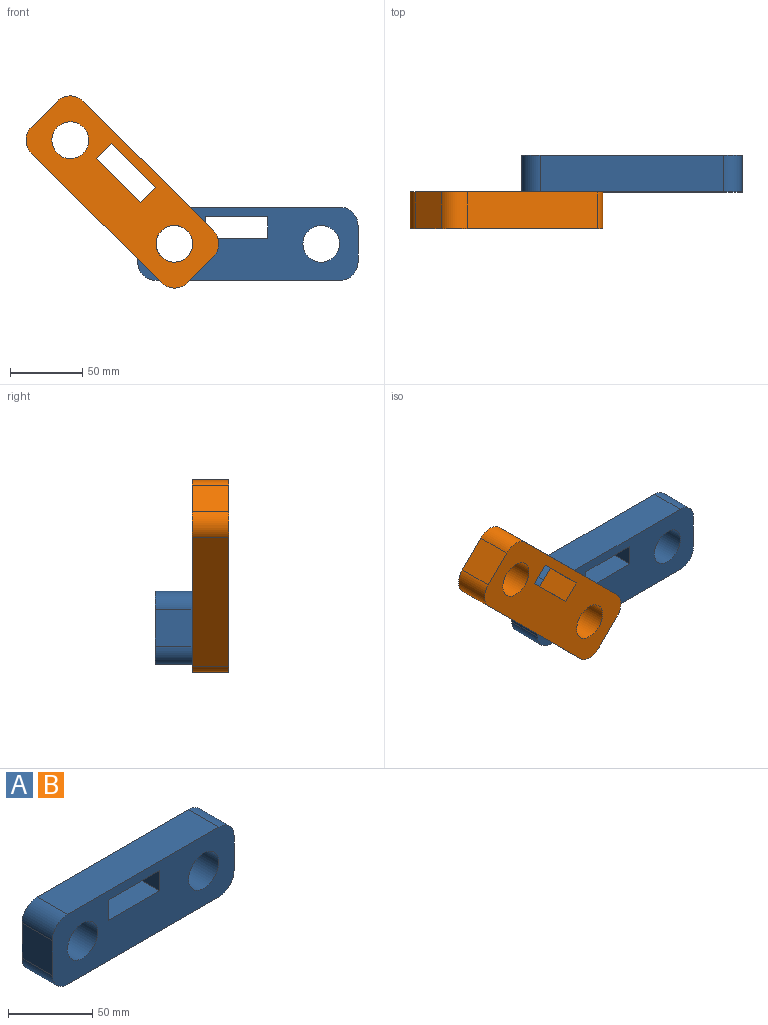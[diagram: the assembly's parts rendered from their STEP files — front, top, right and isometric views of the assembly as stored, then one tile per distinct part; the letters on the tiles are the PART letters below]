
ASSEMBLY  parts=2 mates=1
PART A: 16 faces, bbox 152.4x25.4x50.8 mm
  f0: plane 152.4x50.8mm, normal (0,-1,0), area 5955.5mm2, adj f2,f3,f4,f5,f6,f7,f8,f9
  f1: plane 152.4x50.8mm, normal (0,1,0), area 5955.5mm2, adj f2,f3,f4,f5,f6,f7,f8,f9
  f2: plane 127x25.4mm, normal (0,0,1), area 3225.8mm2, adj f0,f1,f8,f11
  f3: plane 25.4x25.4mm, normal (-1,0,0), area 645.2mm2, adj f0,f1,f8,f9
  f4: plane 127x25.4mm, normal (0,0,-1), area 3225.8mm2, adj f0,f1,f9,f10
  f5: cylinder r=12.7mm len=25.4mm, axis (0,1,0), area 2026.8mm2, adj f0,f1
  f6: cylinder r=12.7mm len=25.4mm, axis (0,1,0), area 2026.8mm2, adj f0,f1
  f7: plane 25.4x25.4mm, normal (1,0,0), area 645.2mm2, adj f0,f1,f10,f11
  f8: cylinder r=12.7mm len=25.4mm, axis (0,-1,0), area 506.7mm2, adj f0,f1,f2,f3
  f9: cylinder r=12.7mm len=25.4mm, axis (0,1,0), area 506.7mm2, adj f0,f1,f3,f4
  f10: cylinder r=12.7mm len=25.4mm, axis (0,-1,0), area 506.7mm2, adj f0,f1,f4,f7
  f11: cylinder r=12.7mm len=25.4mm, axis (0,1,0), area 506.7mm2, adj f0,f1,f2,f7
  f12: plane 42.99x25.4mm, normal (0,0,-1), area 1091.9mm2, adj f0,f1,f13,f15
  f13: plane 25.4x14.76mm, normal (1,0,0), area 374.9mm2, adj f0,f1,f12,f14
  f14: plane 42.99x25.4mm, normal (0,0,1), area 1091.9mm2, adj f0,f1,f13,f15
  f15: plane 25.4x14.76mm, normal (-1,0,0), area 374.9mm2, adj f0,f1,f12,f14
PART B: same geometry as A
PLACE A t=(-37.87,-13.28,12.88)mm fixed
PLACE B rot(axis=(0,1,0),44.9deg) t=(-124.68,-38.68,48.71)mm
MATE revolute A.f5 <-> B.f6  axis (0,1,0) through (-88.67,-25.98,12.88)mm
